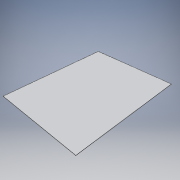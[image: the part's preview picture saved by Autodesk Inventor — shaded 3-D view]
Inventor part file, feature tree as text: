
AUTODESK INVENTOR PART (.ipt)
format: ipt  version: 2019 (Build 230136000, 136)  size: 93,696 bytes
history: native  units: in
note: dims shown in document units (in); Inventor stores cm internally (conversion verified against a paired STEP export)
features: extrude x1, sketch x1
ambient origin geometry x8: Origin, YZ Plane, XZ Plane, XY Plane, X Axis, Y Axis, Z Axis, Center Point
bodies: Solid1 (feature_tree)
feature tree (2):
  extrude  "Extrusion1"  Depth=18.0in
  sketch  "Sketch1"  dims[d0=14.0in d1=18.0in d2=0.0625in d3=0.0in]
